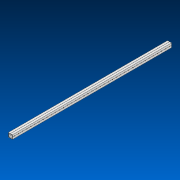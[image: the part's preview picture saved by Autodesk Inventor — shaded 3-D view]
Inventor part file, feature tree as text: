
AUTODESK INVENTOR PART (.ipt)
format: ipt  version: 2022.2 (Build 262287000, 287)  size: 814,080 bytes
history: native  units: in
note: dims shown in document units (in); Inventor stores cm internally (conversion verified against a paired STEP export)
features: other x39, extrude x1, pattern_linear x1, sketch x1, pattern_circular x1
ambient origin geometry x8: Origin, YZ Plane, XZ Plane, XY Plane, X Axis, Y Axis, Z Axis, Center Point
bodies: Solid1 (feature_tree)
feature tree (43):
  extrude  "Extrusion1"  Depth=1.0in
  other  "Work Axis1"
  pattern_linear  "Rectangular Pattern1"  Spacing1=0.0in  [1 undecoded]
  sketch  "Sketch1"  dims[d0=1.0in d1=20.0in d2=0.0in d3=15.3543in d5=1.0in]
  other  "Work Axis2"
  other  "Work Axis3"
  other  "Work Axis4"
  other  "Work Axis5"
  other  "Work Axis6"
  other  "Work Axis7"
  other  "Work Axis8"
  other  "Work Axis9"
  other  "Work Axis10"
  other  "Work Axis11"
  other  "Work Axis12"
  other  "Work Axis13"
  other  "Work Axis14"
  other  "Work Axis15"
  other  "Work Axis16"
  other  "Work Axis17"
  other  "Work Axis18"
  other  "Work Axis19"
  other  "Work Axis20"
  other  "Work Axis21"
  other  "Work Axis22"
  other  "Work Axis23"
  other  "Work Axis24"
  other  "Work Axis25"
  other  "Work Axis26"
  other  "Work Axis27"
  other  "Work Axis28"
  other  "Work Axis29"
  other  "Work Axis30"
  other  "Work Axis31"
  other  "Work Axis32"
  other  "Work Axis33"
  other  "Work Axis34"
  other  "Work Axis35"
  other  "Work Axis36"
  other  "Work Axis37"
  other  "Work Axis38"
  other  "Work Axis39"
  pattern_circular  "CirPattern2"
note: 1 required parameter value undecoded (feature->parameter linkage not recoverable at this tier; creation-order binding heuristic only, values carry confidence <= 0.55)
